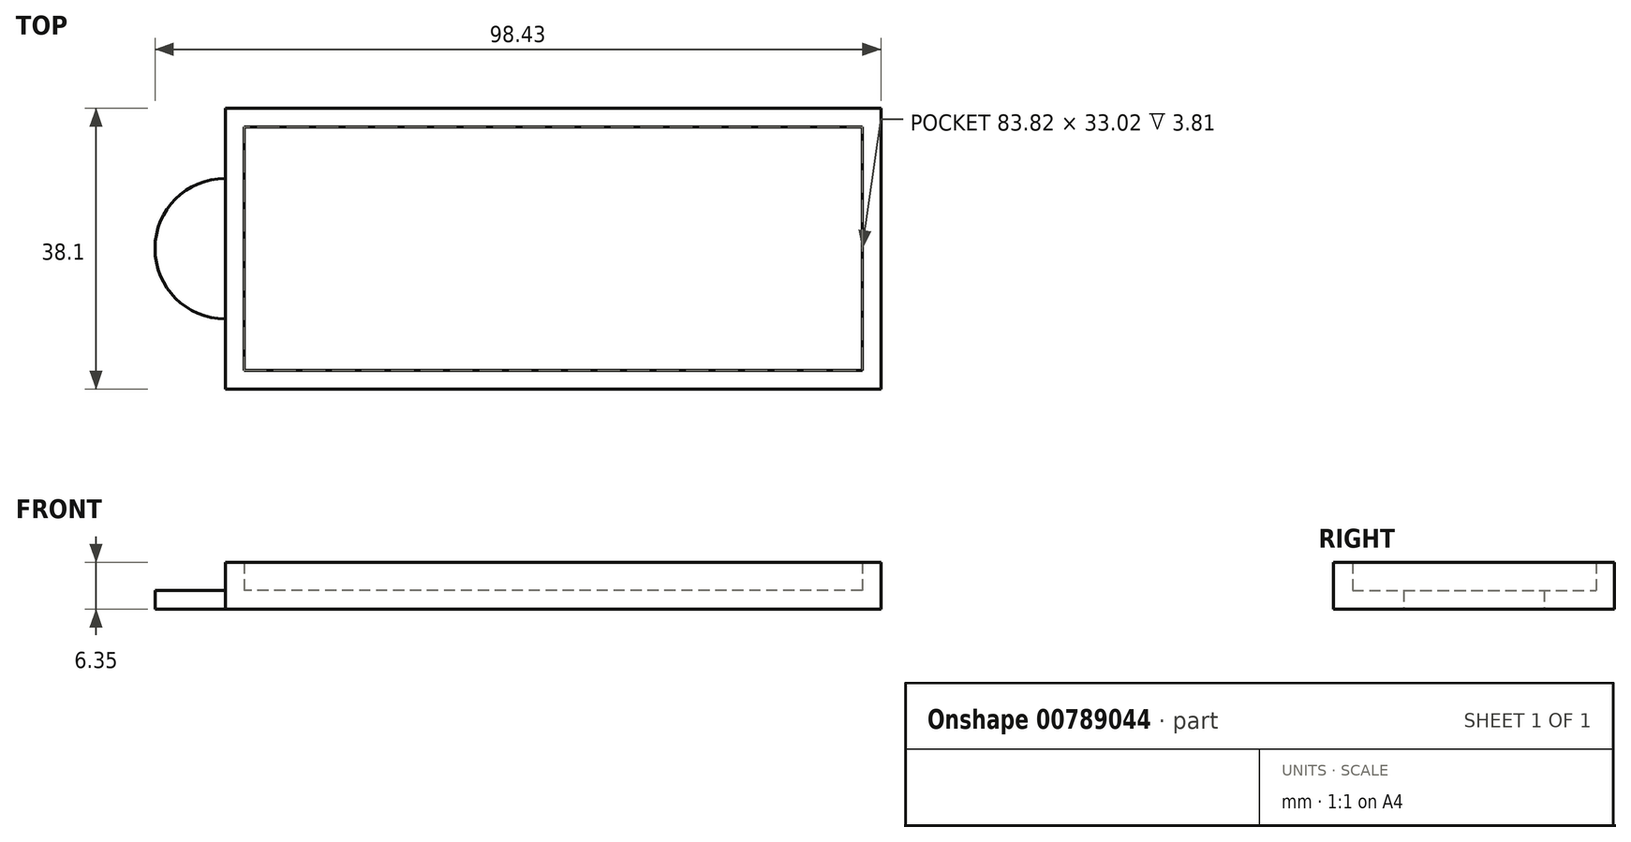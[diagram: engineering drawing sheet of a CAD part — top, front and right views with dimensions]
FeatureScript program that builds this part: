
annotation { "Feature Type Name" : "Feature", "Feature Type Description" : "" }
export const myFeature = defineFeature(function(context is Context, id is Id, definition is map)
    precondition{}
    {
        {
            var Q0;
            Q0=qCreatedBy(makeId("Top.planeOp"),FACE);
            var sketch = newSketch(context, id + "F0", { "sketchPlane" : qUnion([Q0])});
            skLineSegment(sketch, "E0.bottom", {"start": v(44.45, -19.05) * mm, "end": v(-44.45, -19.05) * mm});
            skLineSegment(sketch, "E0.top", {"start": v(44.45, 19.05) * mm, "end": v(-44.45, 19.05) * mm});
            skLineSegment(sketch, "E0.left", {"start": v(44.45, -19.05) * mm, "end": v(44.45, 19.05) * mm});
            skLineSegment(sketch, "E0.right", {"start": v(-44.45, -19.05) * mm, "end": v(-44.45, 19.05) * mm});
            skPoint(sketch, "E0.middle", {"position": v(0, 0) * mm});
            skSolve(sketch);
        }
        {
            var Q0;
            Q0=makeQuery(id+"F0.imprint","IMPRINT",FACE,{"disambiguationData":[TD([[makeQuery(id+"F0.imprint","IMPRINT",EDGE,{"derivedFrom":sQuery(id+"F0.wireOp",EDGE,"E0.bottom")}),-1.0]])]});
            extrude(context, id + "F1", {"entities" : qUnion([Q0]), "depth" : 6.35 * mm, "offsetDistance" : 25.4 * mm});
        }
        {
            var Q0;
            Q0=makeQuery(id+"F1.opExtrude","CAP_FACE",FACE,{"disambiguationData":[OSD([sQuery(id+"F0.wireOp",EDGE,"E0.bottom"),sQuery(id+"F0.wireOp",EDGE,"E0.top"),sQuery(id+"F0.wireOp",EDGE,"E0.left"),sQuery(id+"F0.wireOp",EDGE,"E0.right")])],"isStart":false});
            shell(context, id + "F2", {"entities" : qUnion([Q0]), "thickness" : 2.54 * mm});
        }
        {
            var Q0;
            Q0=makeQuery(id+"F1.opExtrude","CAP_FACE",FACE,{"disambiguationData":[OSD([sQuery(id+"F0.wireOp",EDGE,"E0.bottom"),sQuery(id+"F0.wireOp",EDGE,"E0.top"),sQuery(id+"F0.wireOp",EDGE,"E0.left"),sQuery(id+"F0.wireOp",EDGE,"E0.right")])],"isStart":true});
            var sketch = newSketch(context, id + "F3", { "sketchPlane" : qUnion([Q0])});
            skCircle(sketch, "E1", {"center": v(-44.45, 0) * mm, "radius": 9.53 * mm});
            skSolve(sketch);
        }
        {
            var Q0;
            {var subQ0=sQuery(id+"F3.wireOp",EDGE,"E1");var subQ1=makeQuery(id+"F1.opExtrude","CAP_EDGE",EDGE,{"disambiguationData":[OSD([sQuery(id+"F0.wireOp",EDGE,"E0.right")])],"isStart":true});var subQ2=makeQuery(id+"F3.imprint","INTERSECT",VERTEX,{"disambiguationData":[OD(0.0)],"derivedFrom":[subQ1,subQ0]});Q0=makeQuery(id+"F3.imprint","IMPRINT",FACE,{"disambiguationData":[TD([[makeQuery(id+"F3.imprint","IMPRINT",EDGE,{"disambiguationData":[TD([[subQ2,-1.0]])],"derivedFrom":subQ0}),1.0]])]});}
            extrude(context, id + "F4", {"entities" : qUnion([Q0]), "operationType" : NewBodyOperationType.ADD, "oppositeDirection" : true, "depth" : 2.54 * mm, "offsetDistance" : 25.4 * mm});
        }
    });
